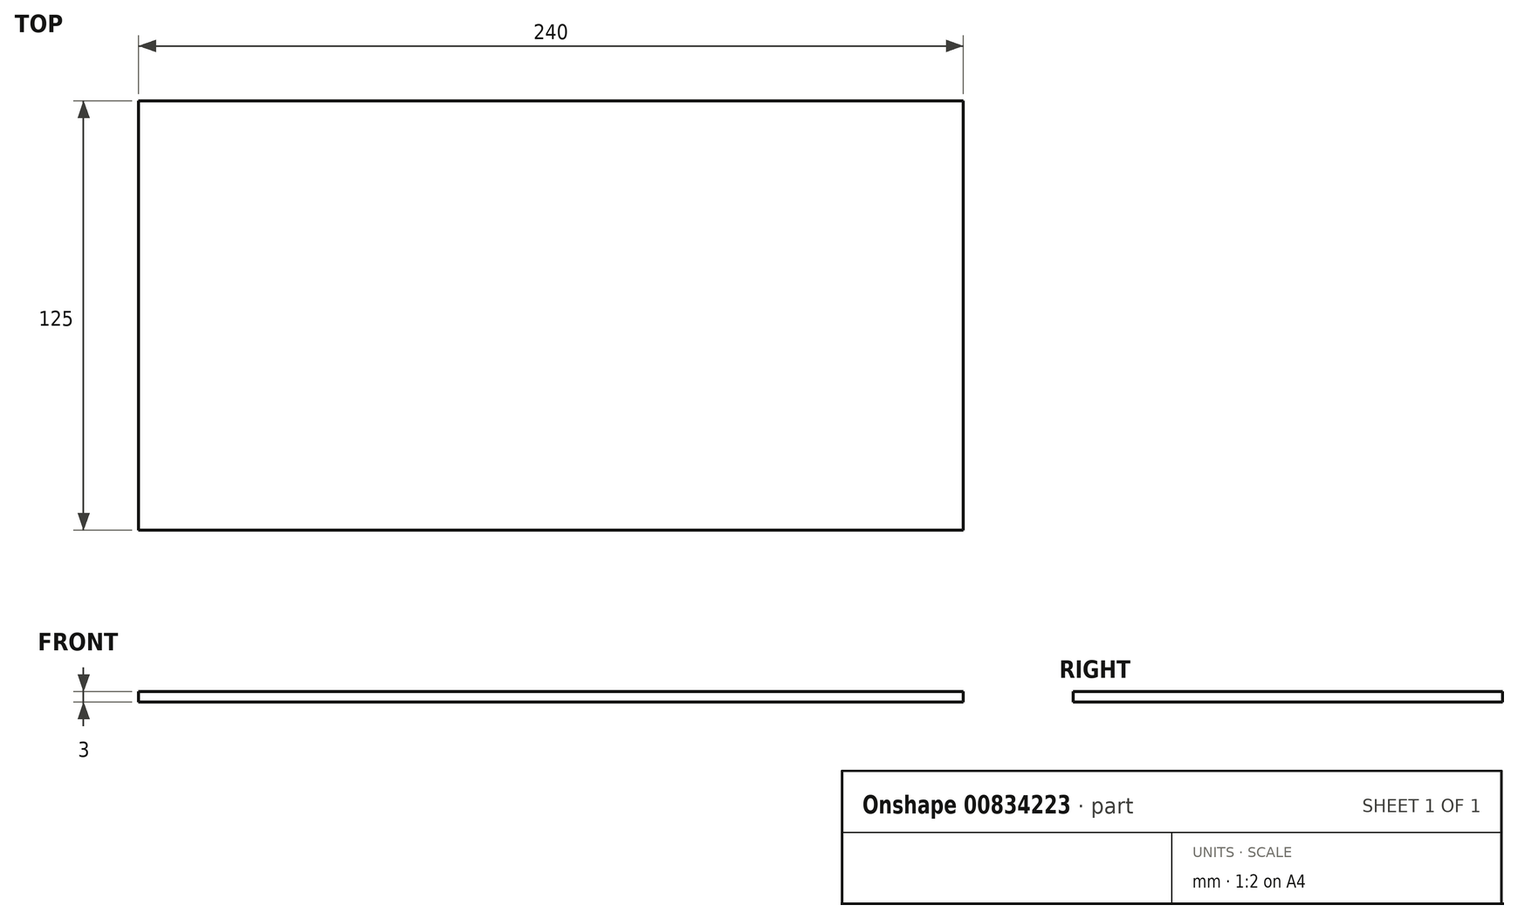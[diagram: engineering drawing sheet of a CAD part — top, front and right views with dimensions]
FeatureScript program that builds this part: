
annotation { "Feature Type Name" : "Feature", "Feature Type Description" : "" }
export const myFeature = defineFeature(function(context is Context, id is Id, definition is map)
    precondition{}
    {
        {
            var Q0;
            Q0=qCreatedBy(makeId("Top.planeOp"),FACE);
            var sketch = newSketch(context, id + "F0", { "sketchPlane" : qUnion([Q0])});
            skLineSegment(sketch, "E0.bottom", {"start": v(0, 0) * mm, "end": v(240, 0) * mm});
            skLineSegment(sketch, "E0.top", {"start": v(0, -125) * mm, "end": v(240, -125) * mm});
            skLineSegment(sketch, "E0.left", {"start": v(0, 0) * mm, "end": v(0, -125) * mm});
            skLineSegment(sketch, "E0.right", {"start": v(240, 0) * mm, "end": v(240, -125) * mm});
            skSolve(sketch);
        }
        {
            var Q0;
            Q0=makeQuery(id+"F0.imprint","IMPRINT",FACE,{"disambiguationData":[TD([[makeQuery(id+"F0.imprint","IMPRINT",EDGE,{"derivedFrom":sQuery(id+"F0.wireOp",EDGE,"E0.bottom")}),-1.0]])]});
            extrude(context, id + "F1", {"entities" : qUnion([Q0]), "depth" : 3 * mm, "offsetDistance" : 25 * mm});
        }
    });
